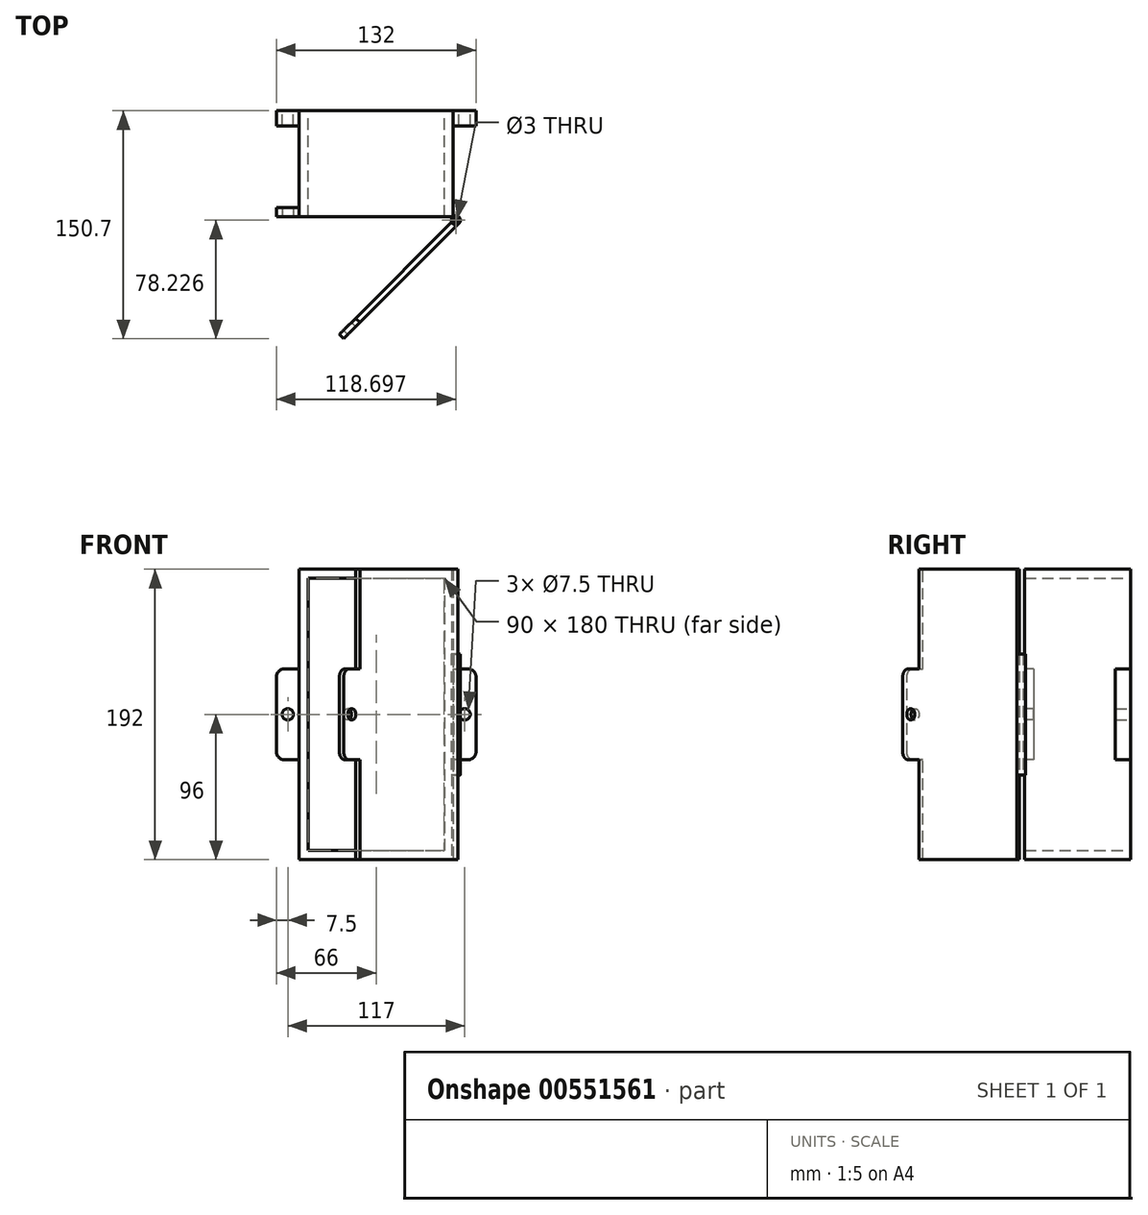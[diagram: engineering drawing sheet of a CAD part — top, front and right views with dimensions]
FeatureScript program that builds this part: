
annotation { "Feature Type Name" : "Feature", "Feature Type Description" : "" }
export const myFeature = defineFeature(function(context is Context, id is Id, definition is map)
    precondition{}
    {
        {
            var Q0;
            Q0=qCreatedBy(makeId("Front.planeOp"),FACE);
            var sketch = newSketch(context, id + "F0", { "sketchPlane" : qUnion([Q0])});
            skLineSegment(sketch, "E0.bottom", {"start": v(-45, 90) * mm, "end": v(45, 90) * mm});
            skLineSegment(sketch, "E0.top", {"start": v(-45, -90) * mm, "end": v(45, -90) * mm});
            skLineSegment(sketch, "E0.left", {"start": v(-45, 90) * mm, "end": v(-45, -90) * mm});
            skLineSegment(sketch, "E0.right", {"start": v(45, 90) * mm, "end": v(45, -90) * mm});
            skLineSegment(sketch, "E1.bottom", {"start": v(-51, 96) * mm, "end": v(51, 96) * mm});
            skLineSegment(sketch, "E1.top", {"start": v(-51, -96) * mm, "end": v(51, -96) * mm});
            skLineSegment(sketch, "E1.left", {"start": v(-51, 96) * mm, "end": v(-51, -96) * mm});
            skLineSegment(sketch, "E1.right", {"start": v(51, 96) * mm, "end": v(51, -96) * mm});
            skLineSegment(sketch, "E2", {"start": v(-51, 30) * mm, "end": v(-66, 30) * mm});
            skLineSegment(sketch, "E3", {"start": v(-66, 30) * mm, "end": v(-66, -30) * mm});
            skLineSegment(sketch, "E4", {"start": v(51, 30) * mm, "end": v(66, 30) * mm});
            skLineSegment(sketch, "E5", {"start": v(66, 30) * mm, "end": v(66, -30) * mm});
            skLineSegment(sketch, "E6", {"start": v(-66, -30) * mm, "end": v(-51, -30) * mm});
            skLineSegment(sketch, "E7", {"start": v(66, -30) * mm, "end": v(51, -30) * mm});
            skCircle(sketch, "E8", {"center": v(-58.5, 0) * mm, "radius": 3.75 * mm});
            skCircle(sketch, "E9", {"center": v(58.5, 0) * mm, "radius": 3.75 * mm});
            skSolve(sketch);
        }
        {
            var Q0;
            Q0=makeQuery(id+"F0.imprint","IMPRINT",FACE,{"disambiguationData":[TD([[makeQuery(id+"F0.imprint","IMPRINT",EDGE,{"derivedFrom":sQuery(id+"F0.wireOp",EDGE,"E0.bottom")}),1.0]])]});
            extrude(context, id + "F1", {"entities" : qUnion([Q0]), "depth" : 70 * mm, "offsetDistance" : 25 * mm});
        }
        {
            var Q0;
            {var subQ1=sQuery(id+"F0.wireOp",EDGE,"E2");Q0=makeQuery(id+"F0.imprint","IMPRINT",FACE,{"disambiguationData":[TD([[makeQuery(id+"F0.imprint","IMPRINT",EDGE,{"derivedFrom":subQ1}),1.0]])]});}
            var Q1;
            {var subQ1=sQuery(id+"F0.wireOp",EDGE,"E4");Q1=makeQuery(id+"F0.imprint","IMPRINT",FACE,{"disambiguationData":[TD([[makeQuery(id+"F0.imprint","IMPRINT",EDGE,{"derivedFrom":subQ1}),-1.0]])]});}
            extrude(context, id + "F2", {"entities" : qUnion([Q0, Q1]), "operationType" : NewBodyOperationType.ADD, "depth" : 10 * mm, "offsetDistance" : 25 * mm});
        }
        {
            var Q0;
            Q0=makeQuery(id+"F2.opExtrude","SWEPT_EDGE",EDGE,{"disambiguationData":[OSD([sQuery(id+"F0.wireOp",EDGE,"E4"),sQuery(id+"F0.wireOp",EDGE,"E5")])]});
            var Q1;
            Q1=makeQuery(id+"F2.opExtrude","SWEPT_EDGE",EDGE,{"disambiguationData":[OSD([sQuery(id+"F0.wireOp",EDGE,"E5"),sQuery(id+"F0.wireOp",EDGE,"E7")])]});
            var Q2;
            Q2=makeQuery(id+"F2.opExtrude","SWEPT_EDGE",EDGE,{"disambiguationData":[OSD([sQuery(id+"F0.wireOp",EDGE,"E3"),sQuery(id+"F0.wireOp",EDGE,"E6")])]});
            var Q3;
            Q3=makeQuery(id+"F2.opExtrude","SWEPT_EDGE",EDGE,{"disambiguationData":[OSD([sQuery(id+"F0.wireOp",EDGE,"E2"),sQuery(id+"F0.wireOp",EDGE,"E3")])]});
            fillet(context, id + "F3", {"entities" : qUnion([Q0, Q1, Q2, Q3]), "radius" : 5 * mm, "tangentPropagation" : true, "allowEdgeOverflow" : false});
        }
        {
            var Q0;
            Q0=makeQuery(id+"F1.opExtrude","CAP_FACE",FACE,{"disambiguationData":[OSD([sQuery(id+"F0.wireOp",EDGE,"E0.bottom"),sQuery(id+"F0.wireOp",EDGE,"E0.top"),sQuery(id+"F0.wireOp",EDGE,"E0.left"),sQuery(id+"F0.wireOp",EDGE,"E0.right"),sQuery(id+"F0.wireOp",EDGE,"E1.bottom"),sQuery(id+"F0.wireOp",EDGE,"E1.top"),sQuery(id+"F0.wireOp",EDGE,"E1.left"),sQuery(id+"F0.wireOp",EDGE,"E1.right")])],"isStart":false});
            var sketch = newSketch(context, id + "F4", { "sketchPlane" : qUnion([Q0])});
            skLineSegment(sketch, "E10", {"start": v(-30, -96) * mm, "end": v(-30, -111) * mm});
            skLineSegment(sketch, "E11", {"start": v(-30, -111) * mm, "end": v(30, -111) * mm});
            skLineSegment(sketch, "E12", {"start": v(-30, -96) * mm, "end": v(30, -96) * mm});
            skLineSegment(sketch, "E13", {"start": v(30, -96) * mm, "end": v(30, -111) * mm});
            skCircle(sketch, "E14", {"center": v(0, -103.5) * mm, "radius": 3.75 * mm});
            skSolve(sketch);
        }
        {
            var Q0;
            Q0=qCreatedBy(makeId("Top.planeOp"),FACE);
            var sketch = newSketch(context, id + "F5", { "sketchPlane" : qUnion([Q0])});
            skCircle(sketch, "E15", {"center": v(52.7, -72.47) * mm, "radius": 3 * mm});
            skCircle(sketch, "E16", {"center": v(52.7, -72.47) * mm, "radius": 1.5 * mm});
            skSolve(sketch);
        }
        {
            var Q0;
            Q0 = qSketchRegion(id + "F5", true);
            extrude(context, id + "F6", {"entities" : qUnion([Q0]), "endBound" : BoundingType.SYMMETRIC, "depth" : 80 * mm, "offsetDistance" : 25 * mm});
        }
        {
            var Q0;
            {var subQ0=sQuery(id+"F4.wireOp",EDGE,"E12");Q0=makeQuery(id+"F4.imprint","IMPRINT",FACE,{"disambiguationData":[TD([[makeQuery(id+"F4.imprint","IMPRINT",EDGE,{"derivedFrom":subQ0}),1.0]])]});}
            var sketch = newSketch(context, id + "F7", { "sketchPlane" : qUnion([Q0])});
            skLineSegment(sketch, "E17", {"start": v(-51, 30) * mm, "end": v(-66, 30) * mm});
            skLineSegment(sketch, "E18", {"start": v(-66, 30) * mm, "end": v(-66, -30) * mm});
            skLineSegment(sketch, "E19", {"start": v(-66, -30) * mm, "end": v(-51, -30) * mm});
            skLineSegment(sketch, "E20", {"start": v(-51, 30) * mm, "end": v(-51, -30) * mm});
            skCircle(sketch, "E21", {"center": v(-58.5, 0) * mm, "radius": 3.75 * mm});
            skSolve(sketch);
        }
        {
            var Q0;
            Q0 = qSketchRegion(id + "F7", true);
            extrude(context, id + "F8", {"entities" : qUnion([Q0]), "oppositeDirection" : true, "depth" : 6 * mm, "offsetDistance" : 25 * mm});
        }
        {
            var Q0;
            Q0=makeQuery(id+"F1.opExtrude","CAP_EDGE",EDGE,{"disambiguationData":[OSD([sQuery(id+"F0.wireOp",EDGE,"E1.left")])],"isStart":false});
            cPlane(context, id + "F9", {"entities" : qUnion([Q0]), "cplaneType" : CPlaneType.LINE_ANGLE, "offset" : 25 * mm, "angle" : 315 * degree, "width" : 150 * mm, "height" : 150 * mm});
        }
        {
            var Q0;
            Q0=qCreatedBy(id+"F9.planeOp",FACE);
            var sketch = newSketch(context, id + "F10", { "sketchPlane" : qUnion([Q0])});
            skLineSegment(sketch, "E22.bottom", {"start": v(91.36, 96) * mm, "end": v(87.36, 96) * mm});
            skLineSegment(sketch, "E22.top", {"start": v(91.36, -96) * mm, "end": v(87.36, -96) * mm});
            skLineSegment(sketch, "E22.left", {"start": v(91.36, 96) * mm, "end": v(91.36, -96) * mm});
            skLineSegment(sketch, "E22.right", {"start": v(87.36, 96) * mm, "end": v(87.36, -96) * mm});
            skSolve(sketch);
        }
        {
            var Q0;
            Q0=makeQuery(id+"F10.imprint","IMPRINT",FACE,{"disambiguationData":[TD([[makeQuery(id+"F10.imprint","IMPRINT",EDGE,{"derivedFrom":sQuery(id+"F10.wireOp",EDGE,"E22.bottom")}),1.0]])]});
            var Q1;
            Q1=makeQuery(id+"F6.opExtrude","SWEPT_FACE",FACE,{"disambiguationData":[OSD([sQuery(id+"F5.wireOp",EDGE,"E15")])]});
            extrude(context, id + "F11", {"entities" : qUnion([Q0]), "operationType" : NewBodyOperationType.ADD, "endBound" : BoundingType.UP_TO_SURFACE, "oppositeDirection" : true, "depth" : 25 * mm, "endBoundEntityFace" : qUnion([Q1]), "offsetDistance" : 25 * mm});
        }
        {
            var Q0;
            Q0=makeQuery(id+"F11.opExtrude","SWEPT_FACE",FACE,{"disambiguationData":[OSD([sQuery(id+"F10.wireOp",EDGE,"E22.right")])]});
            var sketch = newSketch(context, id + "F12", { "sketchPlane" : qUnion([Q0])});
            skLineSegment(sketch, "E23", {"start": v(16.76, -68) * mm, "end": v(16.76, 68) * mm});
            skLineSegment(sketch, "E24", {"start": v(85.56, -96) * mm, "end": v(85.56, 96) * mm});
            skLineSegment(sketch, "E25", {"start": v(85.56, -96) * mm, "end": v(106.76, -96) * mm});
            skLineSegment(sketch, "E26", {"start": v(106.76, -96) * mm, "end": v(106.76, -30) * mm});
            skLineSegment(sketch, "E27", {"start": v(106.76, -30) * mm, "end": v(121.76, -30) * mm});
            skLineSegment(sketch, "E28", {"start": v(121.76, -30) * mm, "end": v(121.76, 30) * mm});
            skLineSegment(sketch, "E29", {"start": v(121.76, 30) * mm, "end": v(106.76, 30) * mm});
            skLineSegment(sketch, "E30.trimOffspring", {"start": v(106.76, 30) * mm, "end": v(106.76, 96) * mm});
            skCircle(sketch, "E31", {"center": v(114.26, 0) * mm, "radius": 3.75 * mm});
            skLineSegment(sketch, "E32", {"start": v(106.76, 96) * mm, "end": v(85.56, 96) * mm});
            skPoint(sketch, "E33.end.orphan", {"position": v(85.56, 99.14) * mm});
            skSolve(sketch);
        }
        {
            var Q0;
            Q0 = qSketchRegion(id + "F12", true);
            extrude(context, id + "F13", {"entities" : qUnion([Q0]), "operationType" : NewBodyOperationType.ADD, "oppositeDirection" : true, "depth" : 4 * mm, "offsetDistance" : 25 * mm});
        }
        {
            var Q0;
            Q0=makeQuery(id+"F13.opExtrude","SWEPT_EDGE",EDGE,{"disambiguationData":[OSD([sQuery(id+"F12.wireOp",EDGE,"E28"),sQuery(id+"F12.wireOp",EDGE,"E29")])]});
            var Q1;
            Q1=makeQuery(id+"F13.opExtrude","SWEPT_EDGE",EDGE,{"disambiguationData":[OSD([sQuery(id+"F12.wireOp",EDGE,"E27"),sQuery(id+"F12.wireOp",EDGE,"E28")])]});
            fillet(context, id + "F14", {"entities" : qUnion([Q0, Q1]), "radius" : 5 * mm, "tangentPropagation" : true, "allowEdgeOverflow" : false});
        }
        {
            var Q0;
            Q0=makeQuery(id+"F8.opExtrude","SWEPT_EDGE",EDGE,{"disambiguationData":[OSD([sQuery(id+"F7.wireOp",EDGE,"E17"),sQuery(id+"F7.wireOp",EDGE,"E18")])]});
            var Q1;
            Q1=makeQuery(id+"F8.opExtrude","SWEPT_EDGE",EDGE,{"disambiguationData":[OSD([sQuery(id+"F7.wireOp",EDGE,"E18"),sQuery(id+"F7.wireOp",EDGE,"E19")])]});
            fillet(context, id + "F15", {"entities" : qUnion([Q0, Q1]), "radius" : 5 * mm, "tangentPropagation" : true, "allowEdgeOverflow" : false});
        }
        {
            var Q0;
            Q0=makeQuery(id+"F6.opExtrude","SWEPT_BODY",BODY,{"disambiguationData":[OSD([sQuery(id+"F5.wireOp",EDGE,"E15"),sQuery(id+"F5.wireOp",EDGE,"E16")])]});
            var Q1;
            Q1=makeQuery(id+"F6.opExtrude","CAP_EDGE",EDGE,{"disambiguationData":[OSD([sQuery(id+"F5.wireOp",EDGE,"E16")])],"isStart":false});
            transform(context, id + "F16", {"entities" : qUnion([Q0]), "transformType" : TransformType.ROTATION, "transformAxis" : qUnion([Q1]), "angle" : 0 * degree, "makeCopy" : false});
        }
    });
